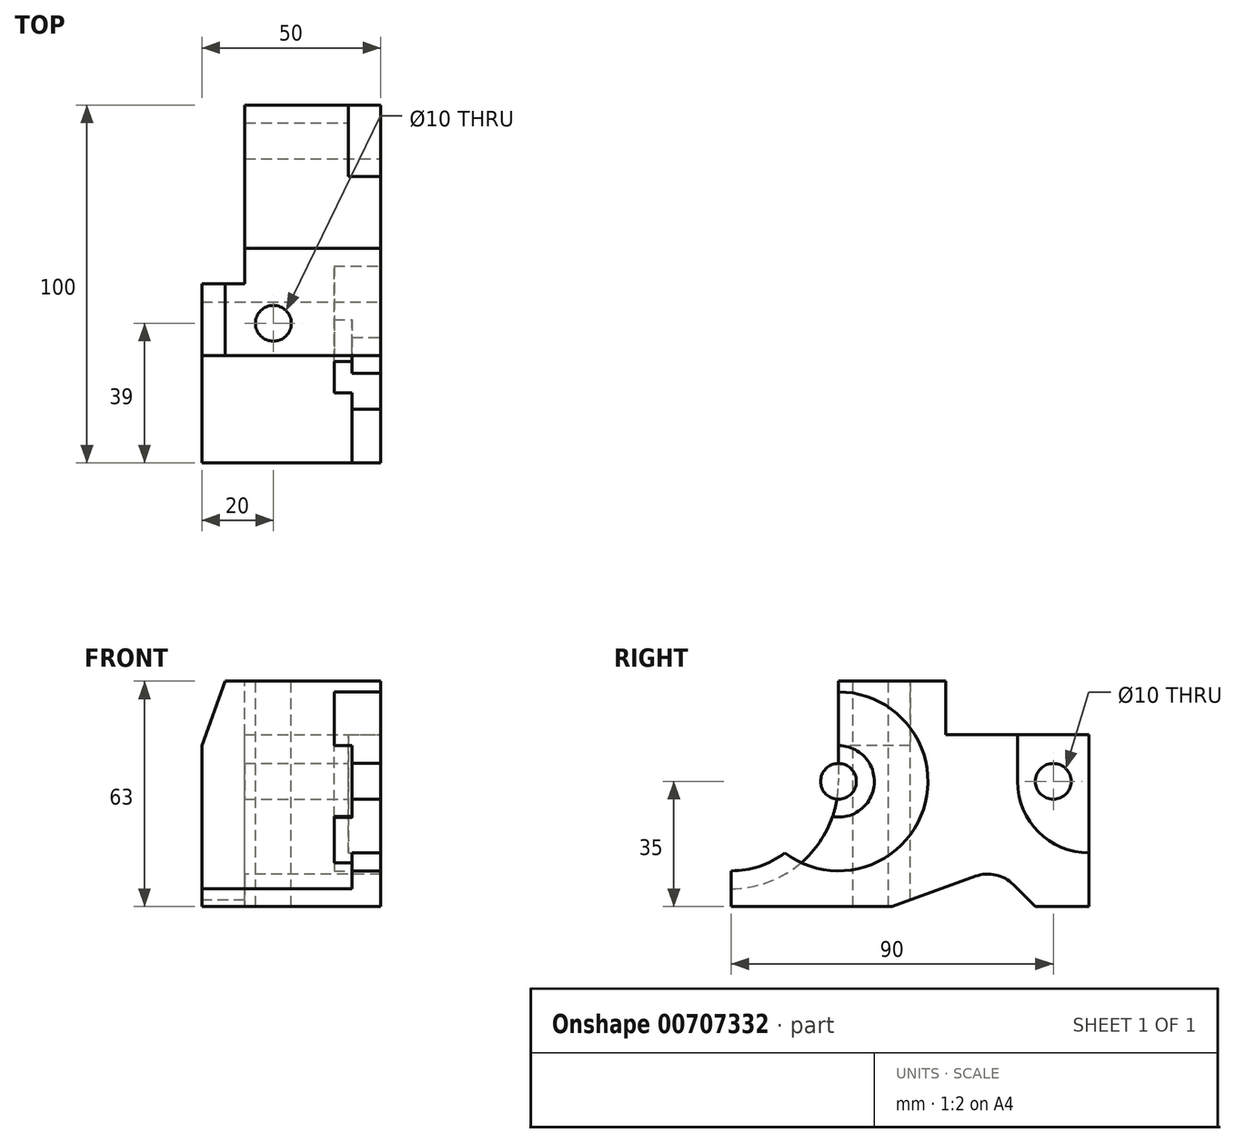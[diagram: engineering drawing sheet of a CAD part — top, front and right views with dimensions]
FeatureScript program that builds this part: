
annotation { "Feature Type Name" : "Feature", "Feature Type Description" : "" }
export const myFeature = defineFeature(function(context is Context, id is Id, definition is map)
    precondition{}
    {
        {
            assignVariable(context, id + "F0", {"name" : "B", "anyValue" : 50});
        }
        {
            var Q0;
            Q0=qCreatedBy(makeId("Right.planeOp"),FACE);
            var sketch = newSketch(context, id + "F1", { "sketchPlane" : qUnion([Q0])});
            skLineSegment(sketch, "E0", {"start": v(0, 0) * mm, "end": v(45, 0) * mm});
            skLineSegment(sketch, "E1", {"start": v(45, 0) * mm, "end": v(74.33, 10.67) * mm});
            skLineSegment(sketch, "E2", {"start": v(74.33, 10.67) * mm, "end": v(85, 0) * mm});
            skLineSegment(sketch, "E3", {"start": v(85, 0) * mm, "end": v(100, 0) * mm});
            skLineSegment(sketch, "E4", {"start": v(100, 0) * mm, "end": v(100, 48) * mm});
            skLineSegment(sketch, "E5", {"start": v(100, 48) * mm, "end": v(60, 48) * mm});
            skLineSegment(sketch, "E6", {"start": v(60, 48) * mm, "end": v(60, 63) * mm});
            skLineSegment(sketch, "E7", {"start": v(60, 63) * mm, "end": v(30, 63) * mm});
            skLineSegment(sketch, "E8", {"start": v(30, 63) * mm, "end": v(30, 35) * mm});
            skLineSegment(sketch, "E9", {"start": v(0, 0) * mm, "end": v(0, 5) * mm});
            skArc(sketch, "E10", {"start": v(0, 5) * mm, "mid": v(21.21, 13.79) * mm, "end": v(30, 35) * mm});
            skSolve(sketch);
        }
        {
            var Q0;
            Q0 = qSketchRegion(id + "F1", true);
            extrude(context, id + "F2", {"entities" : qUnion([Q0]), "oppositeDirection" : true, "depth" : (getVariable(context, 'B')) * mm, "offsetDistance" : 25 * mm});
        }
        {
            var Q0;
            Q0=makeQuery(id+"F2.opExtrude","CAP_FACE",FACE,{"disambiguationData":[OSD([sQuery(id+"F1.wireOp",EDGE,"E0"),sQuery(id+"F1.wireOp",EDGE,"E1"),sQuery(id+"F1.wireOp",EDGE,"E2"),sQuery(id+"F1.wireOp",EDGE,"E3"),sQuery(id+"F1.wireOp",EDGE,"E4"),sQuery(id+"F1.wireOp",EDGE,"E5"),sQuery(id+"F1.wireOp",EDGE,"E6"),sQuery(id+"F1.wireOp",EDGE,"E7"),sQuery(id+"F1.wireOp",EDGE,"E8"),sQuery(id+"F1.wireOp",EDGE,"E9"),sQuery(id+"F1.wireOp",EDGE,"E10")])],"isStart":true});
            var sketch = newSketch(context, id + "F3", { "sketchPlane" : qUnion([Q0])});
            skArc(sketch, "E11", {"start": v(19.58, 12.27) * mm, "mid": v(54.43, 29.67) * mm, "end": v(30, 60) * mm});
            skArc(sketch, "E12", {"start": v(28.33, 25.14) * mm, "mid": v(39.96, 34.16) * mm, "end": v(30, 45) * mm});
            skCircle(sketch, "E13", {"center": v(30, 35) * mm, "radius": 5 * mm});
            skLineSegment(sketch, "E14", {"start": v(80, 48) * mm, "end": v(80, 35) * mm});
            skArc(sketch, "E15", {"start": v(80, 35) * mm, "mid": v(85.86, 20.86) * mm, "end": v(100, 15) * mm});
            skLineSegment(sketch, "E16.0", {"start": v(100, 48) * mm, "end": v(80, 48) * mm});
            skLineSegment(sketch, "E16.1", {"start": v(100, 15) * mm, "end": v(100, 48) * mm});
            skLineSegment(sketch, "E16.2", {"start": v(30, 60) * mm, "end": v(30, 35) * mm});
            skArc(sketch, "E16.3", {"start": v(19.58, 12.27) * mm, "mid": v(27.27, 22.5) * mm, "end": v(30, 35) * mm});
            skCircle(sketch, "E17", {"center": v(90, 35) * mm, "radius": 5 * mm});
            skLineSegment(sketch, "E18", {"start": v(0, 0) * mm, "end": v(0, 10) * mm});
            skArc(sketch, "E19", {"start": v(15, 15) * mm, "mid": v(17.22, 13.51) * mm, "end": v(19.58, 12.27) * mm});
            skArc(sketch, "E20", {"start": v(0, 10) * mm, "mid": v(7.9, 11.28) * mm, "end": v(15, 15) * mm});
            skLineSegment(sketch, "E21", {"start": v(19.58, 12.27) * mm, "end": v(19.58, 0) * mm});
            skLineSegment(sketch, "E22", {"start": v(19.58, 0) * mm, "end": v(0, 0) * mm});
            skSolve(sketch);
        }
        {
            var Q0;
            {var subQ0=sQuery(id+"F3.wireOp",EDGE,"E11");Q0=makeQuery(id+"F3.imprint","IMPRINT",FACE,{"disambiguationData":[TD([[makeQuery(id+"F3.imprint","IMPRINT",EDGE,{"derivedFrom":subQ0}),1.0]])]});}
            extrude(context, id + "F4", {"entities" : qUnion([Q0]), "operationType" : NewBodyOperationType.REMOVE, "oppositeDirection" : true, "depth" : 13 * mm, "offsetDistance" : 25 * mm});
        }
        {
            var Q0;
            {var subQ0=sQuery(id+"F1.wireOp",EDGE,"E8");var subQ1=sQuery(id+"F1.wireOp",EDGE,"E10");Q0=makeQuery(id+"F4.boolean.opBoolean","SPLIT",FACE,{"disambiguationData":[TD([makeQuery(id+"F4.opExtrude","SWEPT_FACE",FACE,{"disambiguationData":[OSD([sQuery(id+"F3.wireOp",EDGE,"E12")])]})])],"derivedFrom":makeQuery(id+"F2.opExtrude","CAP_FACE",FACE,{"disambiguationData":[OSD([sQuery(id+"F1.wireOp",EDGE,"E0"),sQuery(id+"F1.wireOp",EDGE,"E1"),sQuery(id+"F1.wireOp",EDGE,"E2"),sQuery(id+"F1.wireOp",EDGE,"E3"),sQuery(id+"F1.wireOp",EDGE,"E4"),sQuery(id+"F1.wireOp",EDGE,"E5"),sQuery(id+"F1.wireOp",EDGE,"E6"),sQuery(id+"F1.wireOp",EDGE,"E7"),subQ0,sQuery(id+"F1.wireOp",EDGE,"E9"),subQ1])],"isStart":true})});}
            extrude(context, id + "F5", {"entities" : qUnion([Q0]), "operationType" : NewBodyOperationType.REMOVE, "oppositeDirection" : true, "depth" : 8 * mm, "offsetDistance" : 25 * mm});
        }
        {
            var Q0;
            {var subQ0=sQuery(id+"F3.wireOp",EDGE,"E16.2");var subQ1=sQuery(id+"F3.wireOp",EDGE,"E13");var subQ2=makeQuery(id+"F3.imprint","INTERSECT",VERTEX,{"derivedFrom":[subQ1,subQ0]});Q0=makeQuery(id+"F3.imprint","IMPRINT",FACE,{"disambiguationData":[TD([[makeQuery(id+"F3.imprint","IMPRINT",EDGE,{"disambiguationData":[TD([[subQ2,1.0]])],"derivedFrom":subQ1}),1.0]])]});}
            var Q1;
            {var subQ0=sQuery(id+"F3.wireOp",EDGE,"E16.2");var subQ1=sQuery(id+"F3.wireOp",EDGE,"E13");var subQ2=makeQuery(id+"F3.imprint","INTERSECT",VERTEX,{"derivedFrom":[subQ1,subQ0]});Q1=makeQuery(id+"F3.imprint","IMPRINT",FACE,{"disambiguationData":[TD([[makeQuery(id+"F3.imprint","IMPRINT",EDGE,{"disambiguationData":[TD([[subQ2,-1.0]])],"derivedFrom":subQ1}),1.0]])]});}
            var Q2;
            Q2=makeQuery(id+"F5.boolean.opBoolean","COPY",FACE,{"derivedFrom":makeQuery(id+"F5.opExtrude","CAP_FACE",FACE,{"disambiguationData":[OSD([sQuery(id+"F1.wireOp",EDGE,"E0"),sQuery(id+"F1.wireOp",EDGE,"E1"),sQuery(id+"F1.wireOp",EDGE,"E2"),sQuery(id+"F1.wireOp",EDGE,"E3"),sQuery(id+"F1.wireOp",EDGE,"E4"),sQuery(id+"F1.wireOp",EDGE,"E5"),sQuery(id+"F1.wireOp",EDGE,"E6"),sQuery(id+"F1.wireOp",EDGE,"E7"),sQuery(id+"F1.wireOp",EDGE,"E8"),sQuery(id+"F1.wireOp",EDGE,"E9"),sQuery(id+"F1.wireOp",EDGE,"E10")])],"isStart":false})});
            extrude(context, id + "F6", {"entities" : qUnion([Q0, Q1]), "operationType" : NewBodyOperationType.ADD, "endBound" : BoundingType.UP_TO_SURFACE, "oppositeDirection" : true, "depth" : 25 * mm, "endBoundEntityFace" : qUnion([Q2]), "offsetDistance" : 25 * mm});
        }
        {
            var Q0;
            Q0=makeQuery(id+"F3.imprint","IMPRINT",FACE,{"disambiguationData":[TD([[makeQuery(id+"F3.imprint","IMPRINT",EDGE,{"derivedFrom":sQuery(id+"F3.wireOp",EDGE,"E14")}),1.0]])]});
            var Q1;
            Q1=makeQuery(id+"F3.imprint","IMPRINT",FACE,{"disambiguationData":[TD([[makeQuery(id+"F3.imprint","IMPRINT",EDGE,{"derivedFrom":sQuery(id+"F3.wireOp",EDGE,"E17")}),1.0]])]});
            extrude(context, id + "F7", {"entities" : qUnion([Q0, Q1]), "operationType" : NewBodyOperationType.REMOVE, "oppositeDirection" : true, "depth" : 9 * mm, "offsetDistance" : 25 * mm});
        }
        {
            var Q0;
            Q0=makeQuery(id+"F3.imprint","IMPRINT",FACE,{"disambiguationData":[TD([[makeQuery(id+"F3.imprint","IMPRINT",EDGE,{"derivedFrom":sQuery(id+"F3.wireOp",EDGE,"E17")}),1.0]])]});
            extrude(context, id + "F8", {"entities" : qUnion([Q0]), "operationType" : NewBodyOperationType.REMOVE, "endBound" : BoundingType.THROUGH_ALL, "oppositeDirection" : true, "depth" : 25 * mm, "offsetDistance" : 25 * mm});
        }
        {
            var Q0;
            {var subQ4=sQuery(id+"F3.wireOp",EDGE,"E19");Q0=makeQuery(id+"F3.imprint","IMPRINT",FACE,{"disambiguationData":[TD([[makeQuery(id+"F3.imprint","IMPRINT",EDGE,{"derivedFrom":subQ4}),-1.0]])]});}
            extrude(context, id + "F9", {"entities" : qUnion([Q0]), "operationType" : NewBodyOperationType.ADD, "oppositeDirection" : true, "depth" : 8 * mm, "offsetDistance" : 25 * mm});
        }
        {
            var Q0;
            Q0=makeQuery(id+"F2.opExtrude","SWEPT_FACE",FACE,{"disambiguationData":[OSD([sQuery(id+"F1.wireOp",EDGE,"E8")])]});
            var sketch = newSketch(context, id + "F10", { "sketchPlane" : qUnion([Q0])});
            skLineSegment(sketch, "E23", {"start": v(-50, 45) * mm, "end": v(-43.45, 63) * mm});
            skLineSegment(sketch, "E24", {"start": v(-43.45, 63) * mm, "end": v(-50, 63) * mm});
            skLineSegment(sketch, "E25", {"start": v(-50, 63) * mm, "end": v(-50, 45) * mm});
            skSolve(sketch);
        }
        {
            var Q0;
            Q0 = qSketchRegion(id + "F10", true);
            extrude(context, id + "F11", {"entities" : qUnion([Q0]), "operationType" : NewBodyOperationType.REMOVE, "endBound" : BoundingType.THROUGH_ALL, "oppositeDirection" : true, "depth" : 25 * mm, "offsetDistance" : 25 * mm});
        }
        {
            var Q0;
            Q0=makeQuery(id+"F2.opExtrude","SWEPT_FACE",FACE,{"disambiguationData":[OSD([sQuery(id+"F1.wireOp",EDGE,"E7")])]});
            var sketch = newSketch(context, id + "F12", { "sketchPlane" : qUnion([Q0])});
            skCircle(sketch, "E26", {"center": v(-30, 39) * mm, "radius": 5 * mm});
            skLineSegment(sketch, "E27.bottom", {"start": v(-50, 100) * mm, "end": v(-38, 100) * mm});
            skLineSegment(sketch, "E27.top", {"start": v(-50, 50) * mm, "end": v(-38, 50) * mm});
            skLineSegment(sketch, "E27.left", {"start": v(-50, 100) * mm, "end": v(-50, 50) * mm});
            skLineSegment(sketch, "E27.right", {"start": v(-38, 100) * mm, "end": v(-38, 50) * mm});
            skSolve(sketch);
        }
        {
            var Q0;
            {var subQ1=sQuery(id+"F12.wireOp",EDGE,"E27.bottom");Q0=makeQuery(id+"F12.imprint","IMPRINT",FACE,{"disambiguationData":[TD([[makeQuery(id+"F12.imprint","IMPRINT",EDGE,{"derivedFrom":subQ1}),-1.0]])]});}
            var Q1;
            {var subQ0=sQuery(id+"F12.wireOp",EDGE,"E27.right");var subQ1=sQuery(id+"F12.wireOp",EDGE,"E27.top");var subQ2=makeQuery(id+"F12.imprint","INTERSECT",VERTEX,{"derivedFrom":[subQ1,subQ0]});Q1=makeQuery(id+"F12.imprint","IMPRINT",FACE,{"disambiguationData":[TD([[makeQuery(id+"F12.imprint","IMPRINT",EDGE,{"disambiguationData":[TD([[subQ2,1.0]])],"derivedFrom":subQ0}),-1.0]])]});}
            var Q2;
            Q2=makeQuery(id+"F12.imprint","IMPRINT",FACE,{"disambiguationData":[TD([[makeQuery(id+"F12.imprint","IMPRINT",EDGE,{"derivedFrom":sQuery(id+"F12.wireOp",EDGE,"E26")}),1.0]])]});
            extrude(context, id + "F13", {"entities" : qUnion([Q0, Q1, Q2]), "operationType" : NewBodyOperationType.REMOVE, "endBound" : BoundingType.THROUGH_ALL, "oppositeDirection" : true, "depth" : 25 * mm, "offsetDistance" : 25 * mm});
        }
        {
            var Q0;
            Q0=makeQuery(id+"F2.opExtrude","SWEPT_EDGE",EDGE,{"disambiguationData":[OSD([sQuery(id+"F1.wireOp",EDGE,"E1"),sQuery(id+"F1.wireOp",EDGE,"E2")])]});
            fillet(context, id + "F14", {"entities" : qUnion([Q0]), "radius" : 10 * mm, "tangentPropagation" : true, "allowEdgeOverflow" : false});
        }
    });
